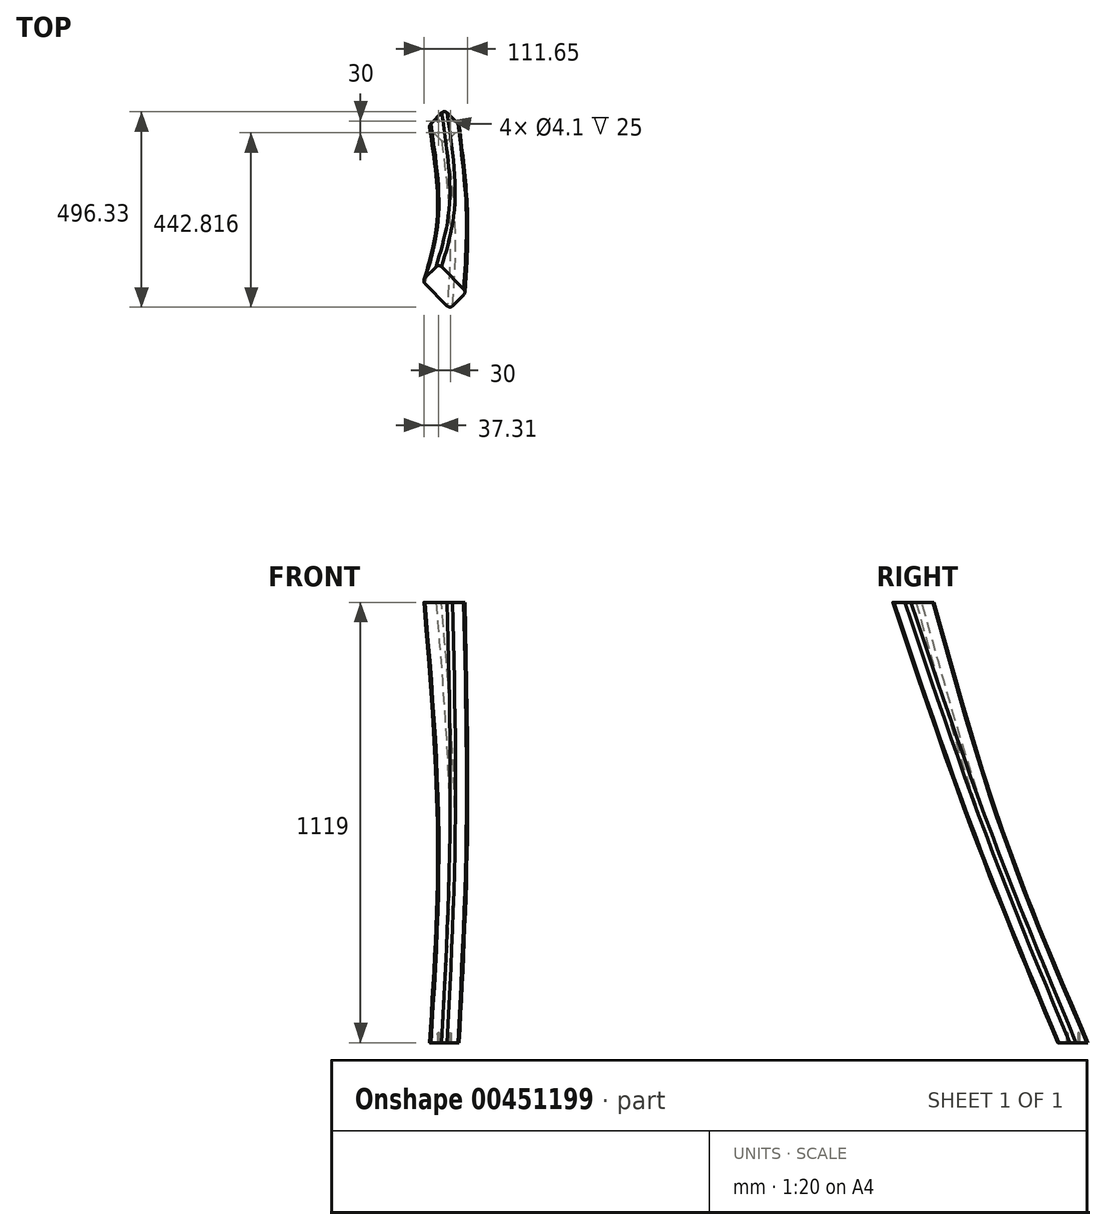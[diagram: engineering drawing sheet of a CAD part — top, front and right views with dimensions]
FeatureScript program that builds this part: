
annotation { "Feature Type Name" : "Feature", "Feature Type Description" : "" }
export const myFeature = defineFeature(function(context is Context, id is Id, definition is map)
    precondition{}
    {
        {
            var Q0;
            Q0=qCreatedBy(makeId("Top.planeOp"),FACE);
            var sketch = newSketch(context, id + "F0", { "sketchPlane" : qUnion([Q0])});
            skLineSegment(sketch, "E0.bottom", {"start": v(0, 0) * mm, "end": v(42.43, 42.43) * mm});
            skLineSegment(sketch, "E0.top", {"start": v(-42.43, 42.43) * mm, "end": v(0, 84.85) * mm});
            skLineSegment(sketch, "E0.left", {"start": v(0, 0) * mm, "end": v(-42.43, 42.43) * mm});
            skLineSegment(sketch, "E0.right", {"start": v(42.43, 42.43) * mm, "end": v(0, 84.85) * mm});
            skSolve(sketch);
        }
        {
            var Q0;
            Q0=qCreatedBy(makeId("Top.planeOp"),FACE);
            cPlane(context, id + "F1", {"entities" : qUnion([Q0]), "cplaneType" : CPlaneType.OFFSET, "offset" : 526 * mm, "width" : 150 * mm, "height" : 150 * mm});
        }
        {
            var Q0;
            Q0=qCreatedBy(makeId("Top.planeOp"),FACE);
            cPlane(context, id + "F2", {"entities" : qUnion([Q0]), "cplaneType" : CPlaneType.OFFSET, "offset" : 1119 * mm, "width" : 150 * mm, "height" : 150 * mm});
        }
        {
            var Q0;
            Q0=qCreatedBy(id+"F1.planeOp",FACE);
            var sketch = newSketch(context, id + "F3", { "sketchPlane" : qUnion([Q0])});
            skLineSegment(sketch, "E1.bottom", {"start": v(63.05, -169.84) * mm, "end": v(20.62, -212.27) * mm});
            skLineSegment(sketch, "E1.top", {"start": v(20.62, -127.42) * mm, "end": v(-21.8, -169.84) * mm});
            skLineSegment(sketch, "E1.left", {"start": v(63.05, -169.84) * mm, "end": v(20.62, -127.42) * mm});
            skLineSegment(sketch, "E1.right", {"start": v(20.62, -212.27) * mm, "end": v(-21.8, -169.84) * mm});
            skPoint(sketch, "E1.middle", {"position": v(20.62, -169.84) * mm});
            skSolve(sketch);
        }
        {
            var Q0;
            Q0=qCreatedBy(id+"F2.planeOp",FACE);
            var sketch = newSketch(context, id + "F4", { "sketchPlane" : qUnion([Q0])});
            skLineSegment(sketch, "E2.bottom", {"start": v(56.57, -376.95) * mm, "end": v(14.14, -419.38) * mm});
            skLineSegment(sketch, "E2.top", {"start": v(-14.14, -306.24) * mm, "end": v(-56.57, -348.67) * mm});
            skLineSegment(sketch, "E2.left", {"start": v(56.57, -376.95) * mm, "end": v(-14.14, -306.24) * mm});
            skLineSegment(sketch, "E2.right", {"start": v(14.14, -419.38) * mm, "end": v(-56.57, -348.67) * mm});
            skPoint(sketch, "E2.middle", {"position": v(0, -362.81) * mm});
            skSolve(sketch);
        }
        {
            var Q0;
            Q0 = qSketchRegion(id + "F0", true);
            var Q1;
            Q1=makeQuery(id+"F3.imprint","IMPRINT",FACE,{"disambiguationData":[TD([[makeQuery(id+"F3.imprint","IMPRINT",EDGE,{"derivedFrom":sQuery(id+"F3.wireOp",EDGE,"E1.bottom")}),-1.0]])]});
            var Q2;
            Q2=makeQuery(id+"F4.imprint","IMPRINT",FACE,{"disambiguationData":[TD([[makeQuery(id+"F4.imprint","IMPRINT",EDGE,{"derivedFrom":sQuery(id+"F4.wireOp",EDGE,"E2.bottom")}),-1.0]])]});
            loft(context, id + "F5", {"sheetProfilesArray" : [{ "sheetProfileEntities" : qUnion([Q0]) }, { "sheetProfileEntities" : qUnion([Q1]) }, { "sheetProfileEntities" : qUnion([Q2]) }]});
        }
        {
            var Q0;
            Q0=makeQuery(id+"F5.opLoft","CAP_FACE",FACE,{"disambiguationData":[OSD([makeQuery(id+"F0.imprint","IMPRINT",FACE,{"disambiguationData":[TD([[makeQuery(id+"F0.imprint","IMPRINT",EDGE,{"derivedFrom":sQuery(id+"F0.wireOp",EDGE,"E0.bottom")}),1.0]])]})])],"isStart":true});
            var sketch = newSketch(context, id + "F6", { "sketchPlane" : qUnion([Q0])});
            skCircle(sketch, "E3", {"center": v(-15, -27.43) * mm, "radius": 2.05 * mm});
            skCircle(sketch, "E4", {"center": v(15, -27.43) * mm, "radius": 2.05 * mm});
            skCircle(sketch, "E5", {"center": v(-15, -57.43) * mm, "radius": 2.05 * mm});
            skCircle(sketch, "E6", {"center": v(15, -57.43) * mm, "radius": 2.05 * mm});
            skLineSegment(sketch, "E7", {"start": v(-21.21, -21.21) * mm, "end": v(21.21, -63.64) * mm, "construction": true});
            skLineSegment(sketch, "E8", {"start": v(-21.21, -63.64) * mm, "end": v(21.21, -21.21) * mm, "construction": true});
            skSolve(sketch);
        }
        {
            var Q0;
            Q0 = qSketchRegion(id + "F6", true);
            extrude(context, id + "F7", {"entities" : qUnion([Q0]), "operationType" : NewBodyOperationType.REMOVE, "oppositeDirection" : true, "depth" : 25 * mm, "offsetDistance" : 25 * mm});
        }
        {
            var Q0;
            Q0=makeQuery(id+"F5.opLoft","SWEPT_EDGE",EDGE,{"disambiguationData":[OSD([sQuery(id+"F0.wireOp",EDGE,"E0.bottom"),sQuery(id+"F0.wireOp",EDGE,"E0.left"),sQuery(id+"F3.wireOp",EDGE,"E1.bottom"),sQuery(id+"F3.wireOp",EDGE,"E1.right"),sQuery(id+"F4.wireOp",EDGE,"E2.bottom"),sQuery(id+"F4.wireOp",EDGE,"E2.right")])]});
            var Q1;
            Q1=makeQuery(id+"F5.opLoft","SWEPT_EDGE",EDGE,{"disambiguationData":[OSD([sQuery(id+"F0.wireOp",EDGE,"E0.top"),sQuery(id+"F0.wireOp",EDGE,"E0.left"),sQuery(id+"F3.wireOp",EDGE,"E1.top"),sQuery(id+"F3.wireOp",EDGE,"E1.right"),sQuery(id+"F4.wireOp",EDGE,"E2.top"),sQuery(id+"F4.wireOp",EDGE,"E2.right")])]});
            var Q2;
            Q2=makeQuery(id+"F5.opLoft","SWEPT_EDGE",EDGE,{"disambiguationData":[OSD([sQuery(id+"F0.wireOp",EDGE,"E0.bottom"),sQuery(id+"F0.wireOp",EDGE,"E0.right"),sQuery(id+"F3.wireOp",EDGE,"E1.bottom"),sQuery(id+"F3.wireOp",EDGE,"E1.left"),sQuery(id+"F4.wireOp",EDGE,"E2.bottom"),sQuery(id+"F4.wireOp",EDGE,"E2.left")])]});
            var Q3;
            Q3=makeQuery(id+"F5.opLoft","SWEPT_EDGE",EDGE,{"disambiguationData":[OSD([sQuery(id+"F0.wireOp",EDGE,"E0.top"),sQuery(id+"F0.wireOp",EDGE,"E0.right"),sQuery(id+"F3.wireOp",EDGE,"E1.top"),sQuery(id+"F3.wireOp",EDGE,"E1.left"),sQuery(id+"F4.wireOp",EDGE,"E2.top"),sQuery(id+"F4.wireOp",EDGE,"E2.left")])]});
            fillet(context, id + "F8", {"entities" : qUnion([Q0, Q1, Q2, Q3]), "tangentPropagation" : true, "radius" : 10 * mm, "defaultsChanged" : false, "vertexSettings" : [], "allowEdgeOverflow" : false});
        }
    });
